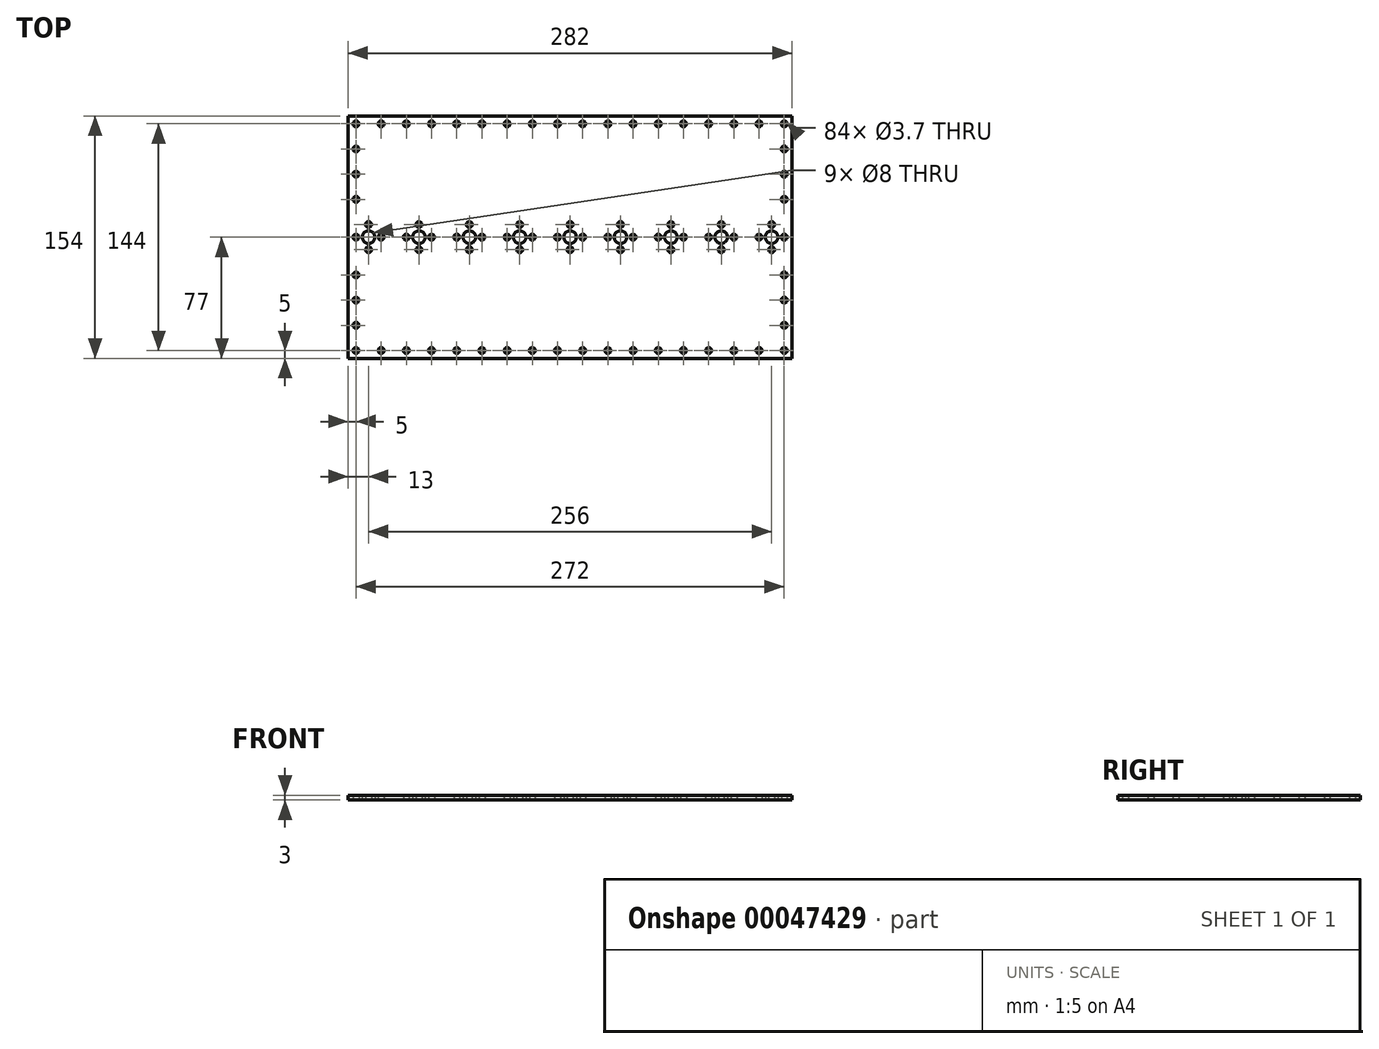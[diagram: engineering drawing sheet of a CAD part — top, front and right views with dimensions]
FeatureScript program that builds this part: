
annotation { "Feature Type Name" : "Feature", "Feature Type Description" : "" }
export const myFeature = defineFeature(function(context is Context, id is Id, definition is map)
    precondition{}
    {
        {
            var Q0;
            Q0=qCreatedBy(makeId("Top.planeOp"),FACE);
            var sketch = newSketch(context, id + "F0", { "sketchPlane" : qUnion([Q0])});
            skLineSegment(sketch, "E0.rect.bottom", {"start": v(-141, -77) * mm, "end": v(141, -77) * mm});
            skLineSegment(sketch, "E0.rect.top", {"start": v(-141, 77) * mm, "end": v(141, 77) * mm});
            skLineSegment(sketch, "E0.rect.left", {"start": v(-141, -77) * mm, "end": v(-141, 77) * mm});
            skLineSegment(sketch, "E0.rect.right", {"start": v(141, -77) * mm, "end": v(141, 77) * mm});
            skPoint(sketch, "E0.rect.middle", {"position": v(0, 0) * mm});
            skCircle(sketch, "E1", {"center": v(0, 0) * mm, "radius": 4 * mm});
            skCircle(sketch, "E2", {"center": v(0, -8) * mm, "radius": 1.85 * mm});
            skCircle(sketch, "E3.1.0", {"center": v(8, 0) * mm, "radius": 1.85 * mm});
            skCircle(sketch, "E3.2.0", {"center": v(0, 8) * mm, "radius": 1.85 * mm});
            skCircle(sketch, "E3.3.0", {"center": v(-8, 0) * mm, "radius": 1.85 * mm});
            skPoint(sketch, "E4.1.0.0", {"position": v(32, 0) * mm});
            skCircle(sketch, "E4.1.0.1", {"center": v(32, 0) * mm, "radius": 4 * mm});
            skCircle(sketch, "E4.1.0.2", {"center": v(40, 0) * mm, "radius": 1.85 * mm});
            skCircle(sketch, "E4.1.0.3", {"center": v(32, 8) * mm, "radius": 1.85 * mm});
            skPoint(sketch, "E4.1.0.4", {"position": v(32, 0) * mm});
            skCircle(sketch, "E4.1.0.5", {"center": v(24, 0) * mm, "radius": 1.85 * mm});
            skCircle(sketch, "E4.1.0.6", {"center": v(32, -8) * mm, "radius": 1.85 * mm});
            skPoint(sketch, "E4.2.0.0", {"position": v(64, 0) * mm});
            skCircle(sketch, "E4.2.0.1", {"center": v(64, 0) * mm, "radius": 4 * mm});
            skCircle(sketch, "E4.2.0.2", {"center": v(72, 0) * mm, "radius": 1.85 * mm});
            skCircle(sketch, "E4.2.0.3", {"center": v(64, 8) * mm, "radius": 1.85 * mm});
            skPoint(sketch, "E4.2.0.4", {"position": v(64, 0) * mm});
            skCircle(sketch, "E4.2.0.5", {"center": v(56, 0) * mm, "radius": 1.85 * mm});
            skCircle(sketch, "E4.2.0.6", {"center": v(64, -8) * mm, "radius": 1.85 * mm});
            skPoint(sketch, "E4.3.0.0", {"position": v(96, 0) * mm});
            skCircle(sketch, "E4.3.0.1", {"center": v(96, 0) * mm, "radius": 4 * mm});
            skCircle(sketch, "E4.3.0.2", {"center": v(104, 0) * mm, "radius": 1.85 * mm});
            skCircle(sketch, "E4.3.0.3", {"center": v(96, 8) * mm, "radius": 1.85 * mm});
            skPoint(sketch, "E4.3.0.4", {"position": v(96, 0) * mm});
            skCircle(sketch, "E4.3.0.5", {"center": v(88, 0) * mm, "radius": 1.85 * mm});
            skCircle(sketch, "E4.3.0.6", {"center": v(96, -8) * mm, "radius": 1.85 * mm});
            skPoint(sketch, "E4.4.0.0", {"position": v(128, 0) * mm});
            skCircle(sketch, "E4.4.0.1", {"center": v(128, 0) * mm, "radius": 4 * mm});
            skCircle(sketch, "E4.4.0.2", {"center": v(136, 0) * mm, "radius": 1.85 * mm});
            skCircle(sketch, "E4.4.0.3", {"center": v(128, 8) * mm, "radius": 1.85 * mm});
            skPoint(sketch, "E4.4.0.4", {"position": v(128, 0) * mm});
            skCircle(sketch, "E4.4.0.5", {"center": v(120, 0) * mm, "radius": 1.85 * mm});
            skCircle(sketch, "E4.4.0.6", {"center": v(128, -8) * mm, "radius": 1.85 * mm});
            skLineSegment(sketch, "E4.direction1", {"start": v(0, 0) * mm, "end": v(32, 0) * mm, "construction": true});
            skCircle(sketch, "E5.1.0.0", {"center": v(-32, 0) * mm, "radius": 4 * mm});
            skCircle(sketch, "E5.1.0.1", {"center": v(-32, -8) * mm, "radius": 1.85 * mm});
            skCircle(sketch, "E5.1.0.2", {"center": v(-24, 0) * mm, "radius": 1.85 * mm});
            skCircle(sketch, "E5.1.0.3", {"center": v(-32, 8) * mm, "radius": 1.85 * mm});
            skCircle(sketch, "E5.1.0.4", {"center": v(-40, 0) * mm, "radius": 1.85 * mm});
            skPoint(sketch, "E5.1.0.5", {"position": v(-32, 0) * mm});
            skPoint(sketch, "E5.1.0.6", {"position": v(-32, 0) * mm});
            skCircle(sketch, "E5.2.0.0", {"center": v(-64, 0) * mm, "radius": 4 * mm});
            skCircle(sketch, "E5.2.0.1", {"center": v(-64, -8) * mm, "radius": 1.85 * mm});
            skCircle(sketch, "E5.2.0.2", {"center": v(-56, 0) * mm, "radius": 1.85 * mm});
            skCircle(sketch, "E5.2.0.3", {"center": v(-64, 8) * mm, "radius": 1.85 * mm});
            skCircle(sketch, "E5.2.0.4", {"center": v(-72, 0) * mm, "radius": 1.85 * mm});
            skPoint(sketch, "E5.2.0.5", {"position": v(-64, 0) * mm});
            skPoint(sketch, "E5.2.0.6", {"position": v(-64, 0) * mm});
            skCircle(sketch, "E5.3.0.0", {"center": v(-96, 0) * mm, "radius": 4 * mm});
            skCircle(sketch, "E5.3.0.1", {"center": v(-96, -8) * mm, "radius": 1.85 * mm});
            skCircle(sketch, "E5.3.0.2", {"center": v(-88, 0) * mm, "radius": 1.85 * mm});
            skCircle(sketch, "E5.3.0.3", {"center": v(-96, 8) * mm, "radius": 1.85 * mm});
            skCircle(sketch, "E5.3.0.4", {"center": v(-104, 0) * mm, "radius": 1.85 * mm});
            skPoint(sketch, "E5.3.0.5", {"position": v(-96, 0) * mm});
            skPoint(sketch, "E5.3.0.6", {"position": v(-96, 0) * mm});
            skCircle(sketch, "E5.4.0.0", {"center": v(-128, 0) * mm, "radius": 4 * mm});
            skCircle(sketch, "E5.4.0.1", {"center": v(-128, -8) * mm, "radius": 1.85 * mm});
            skCircle(sketch, "E5.4.0.2", {"center": v(-120, 0) * mm, "radius": 1.85 * mm});
            skCircle(sketch, "E5.4.0.3", {"center": v(-128, 8) * mm, "radius": 1.85 * mm});
            skCircle(sketch, "E5.4.0.4", {"center": v(-136, 0) * mm, "radius": 1.85 * mm});
            skPoint(sketch, "E5.4.0.5", {"position": v(-128, 0) * mm});
            skPoint(sketch, "E5.4.0.6", {"position": v(-128, 0) * mm});
            skLineSegment(sketch, "E5.direction1", {"start": v(0, 0) * mm, "end": v(-32, 0) * mm, "construction": true});
            skLineSegment(sketch, "E6", {"start": v(-136, 0) * mm, "end": v(-136, -72) * mm, "construction": true});
            skCircle(sketch, "E7", {"center": v(-136, -72) * mm, "radius": 1.85 * mm});
            skCircle(sketch, "E8.1.0.0", {"center": v(-120, -72) * mm, "radius": 1.85 * mm});
            skCircle(sketch, "E8.2.0.0", {"center": v(-104, -72) * mm, "radius": 1.85 * mm});
            skCircle(sketch, "E8.3.0.0", {"center": v(-88, -72) * mm, "radius": 1.85 * mm});
            skCircle(sketch, "E8.4.0.0", {"center": v(-72, -72) * mm, "radius": 1.85 * mm});
            skCircle(sketch, "E8.5.0.0", {"center": v(-56, -72) * mm, "radius": 1.85 * mm});
            skCircle(sketch, "E8.6.0.0", {"center": v(-40, -72) * mm, "radius": 1.85 * mm});
            skCircle(sketch, "E8.7.0.0", {"center": v(-24, -72) * mm, "radius": 1.85 * mm});
            skCircle(sketch, "E8.8.0.0", {"center": v(-8, -72) * mm, "radius": 1.85 * mm});
            skCircle(sketch, "E8.9.0.0", {"center": v(8, -72) * mm, "radius": 1.85 * mm});
            skCircle(sketch, "E8.10.0.0", {"center": v(24, -72) * mm, "radius": 1.85 * mm});
            skCircle(sketch, "E8.11.0.0", {"center": v(40, -72) * mm, "radius": 1.85 * mm});
            skCircle(sketch, "E8.12.0.0", {"center": v(56, -72) * mm, "radius": 1.85 * mm});
            skCircle(sketch, "E8.13.0.0", {"center": v(72, -72) * mm, "radius": 1.85 * mm});
            skCircle(sketch, "E8.14.0.0", {"center": v(88, -72) * mm, "radius": 1.85 * mm});
            skCircle(sketch, "E8.15.0.0", {"center": v(104, -72) * mm, "radius": 1.85 * mm});
            skCircle(sketch, "E8.16.0.0", {"center": v(120, -72) * mm, "radius": 1.85 * mm});
            skCircle(sketch, "E8.17.0.0", {"center": v(136, -72) * mm, "radius": 1.85 * mm});
            skLineSegment(sketch, "E8.direction1", {"start": v(-136, -72) * mm, "end": v(-120, -72) * mm, "construction": true});
            skLineSegment(sketch, "E9", {"start": v(-136, 0) * mm, "end": v(-136, 72) * mm, "construction": true});
            skCircle(sketch, "E10", {"center": v(-136, 72) * mm, "radius": 1.85 * mm});
            skCircle(sketch, "E11.1.0.0", {"center": v(-120, 72) * mm, "radius": 1.85 * mm});
            skCircle(sketch, "E11.2.0.0", {"center": v(-104, 72) * mm, "radius": 1.85 * mm});
            skCircle(sketch, "E11.3.0.0", {"center": v(-88, 72) * mm, "radius": 1.85 * mm});
            skCircle(sketch, "E11.4.0.0", {"center": v(-72, 72) * mm, "radius": 1.85 * mm});
            skCircle(sketch, "E11.5.0.0", {"center": v(-56, 72) * mm, "radius": 1.85 * mm});
            skCircle(sketch, "E11.6.0.0", {"center": v(-40, 72) * mm, "radius": 1.85 * mm});
            skCircle(sketch, "E11.7.0.0", {"center": v(-24, 72) * mm, "radius": 1.85 * mm});
            skCircle(sketch, "E11.8.0.0", {"center": v(-8, 72) * mm, "radius": 1.85 * mm});
            skCircle(sketch, "E11.9.0.0", {"center": v(8, 72) * mm, "radius": 1.85 * mm});
            skCircle(sketch, "E11.10.0.0", {"center": v(24, 72) * mm, "radius": 1.85 * mm});
            skCircle(sketch, "E11.11.0.0", {"center": v(40, 72) * mm, "radius": 1.85 * mm});
            skCircle(sketch, "E11.12.0.0", {"center": v(56, 72) * mm, "radius": 1.85 * mm});
            skCircle(sketch, "E11.13.0.0", {"center": v(72, 72) * mm, "radius": 1.85 * mm});
            skCircle(sketch, "E11.14.0.0", {"center": v(88, 72) * mm, "radius": 1.85 * mm});
            skCircle(sketch, "E11.15.0.0", {"center": v(104, 72) * mm, "radius": 1.85 * mm});
            skCircle(sketch, "E11.16.0.0", {"center": v(120, 72) * mm, "radius": 1.85 * mm});
            skCircle(sketch, "E11.17.0.0", {"center": v(136, 72) * mm, "radius": 1.85 * mm});
            skLineSegment(sketch, "E11.direction1", {"start": v(-136, 72) * mm, "end": v(-120, 72) * mm, "construction": true});
            skCircle(sketch, "E12.0.1.0", {"center": v(136, -56) * mm, "radius": 1.85 * mm});
            skCircle(sketch, "E12.0.2.0", {"center": v(136, -40) * mm, "radius": 1.85 * mm});
            skCircle(sketch, "E12.0.3.0", {"center": v(136, -24) * mm, "radius": 1.85 * mm});
            skLineSegment(sketch, "E12.direction1", {"start": v(136, -72) * mm, "end": v(161, -72) * mm, "construction": true});
            skLineSegment(sketch, "E12.direction2", {"start": v(136, -72) * mm, "end": v(136, -56) * mm, "construction": true});
            skCircle(sketch, "E13.0.1.0", {"center": v(136, 56) * mm, "radius": 1.85 * mm});
            skCircle(sketch, "E13.0.2.0", {"center": v(136, 40) * mm, "radius": 1.85 * mm});
            skCircle(sketch, "E13.0.3.0", {"center": v(136, 24) * mm, "radius": 1.85 * mm});
            skLineSegment(sketch, "E13.direction1", {"start": v(136, 72) * mm, "end": v(152, 72) * mm, "construction": true});
            skLineSegment(sketch, "E13.direction2", {"start": v(136, 72) * mm, "end": v(136, 56) * mm, "construction": true});
            skCircle(sketch, "E14.0.1.0", {"center": v(-136, 56) * mm, "radius": 1.85 * mm});
            skCircle(sketch, "E14.0.2.0", {"center": v(-136, 40) * mm, "radius": 1.85 * mm});
            skCircle(sketch, "E14.0.3.0", {"center": v(-136, 24) * mm, "radius": 1.85 * mm});
            skLineSegment(sketch, "E14.direction1", {"start": v(-136, 72) * mm, "end": v(-111, 72) * mm, "construction": true});
            skLineSegment(sketch, "E14.direction2", {"start": v(-136, 72) * mm, "end": v(-136, 56) * mm, "construction": true});
            skCircle(sketch, "E15.0.1.0", {"center": v(-136, -56) * mm, "radius": 1.85 * mm});
            skCircle(sketch, "E15.0.2.0", {"center": v(-136, -40) * mm, "radius": 1.85 * mm});
            skCircle(sketch, "E15.0.3.0", {"center": v(-136, -24) * mm, "radius": 1.85 * mm});
            skLineSegment(sketch, "E15.direction1", {"start": v(-136, -72) * mm, "end": v(-111, -72) * mm, "construction": true});
            skLineSegment(sketch, "E15.direction2", {"start": v(-136, -72) * mm, "end": v(-136, -56) * mm, "construction": true});
            skSolve(sketch);
        }
        {
            var Q0;
            Q0=makeQuery(id+"F0.imprint","IMPRINT",FACE,{"disambiguationData":[TD([[makeQuery(id+"F0.imprint","IMPRINT",EDGE,{"derivedFrom":sQuery(id+"F0.wireOp",EDGE,"E0.rect.bottom")}),1.0]])]});
            extrude(context, id + "F1", {"entities" : qUnion([Q0]), "depth" : 3 * mm});
        }
    });
